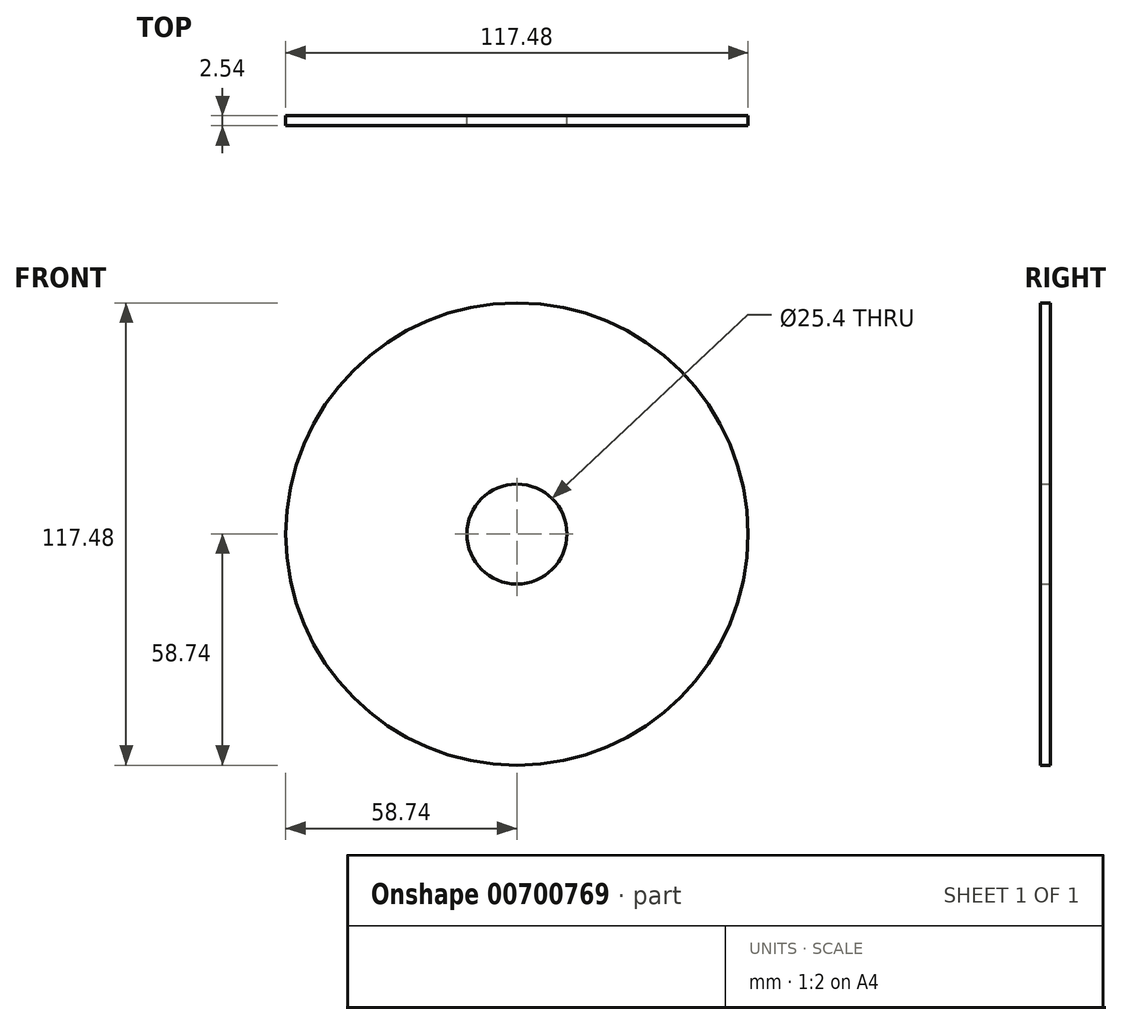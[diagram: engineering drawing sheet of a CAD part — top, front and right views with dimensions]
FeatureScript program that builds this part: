
annotation { "Feature Type Name" : "Feature", "Feature Type Description" : "" }
export const myFeature = defineFeature(function(context is Context, id is Id, definition is map)
    precondition{}
    {
        {
            var Q0;
            Q0=qCreatedBy(makeId("Front.planeOp"),FACE);
            var sketch = newSketch(context, id + "F0", { "sketchPlane" : qUnion([Q0])});
            skCircle(sketch, "E0", {"center": v(0, 0) * mm, "radius": 58.74 * mm});
            skCircle(sketch, "E1", {"center": v(0, 0) * mm, "radius": 12.7 * mm});
            skSolve(sketch);
        }
        {
            var Q0;
            Q0=makeQuery(id+"F0.imprint","IMPRINT",FACE,{"disambiguationData":[TD([[makeQuery(id+"F0.imprint","IMPRINT",EDGE,{"derivedFrom":sQuery(id+"F0.wireOp",EDGE,"E0")}),1.0]])]});
            extrude(context, id + "F1", {"entities" : qUnion([Q0]), "endBound" : BoundingType.SYMMETRIC, "depth" : 2.54 * mm, "offsetDistance" : 25.4 * mm});
        }
    });
